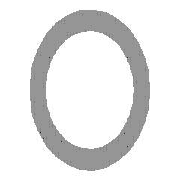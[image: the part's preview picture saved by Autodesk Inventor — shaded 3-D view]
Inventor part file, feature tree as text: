
AUTODESK INVENTOR PART (.ipt)
format: ipt  version: 2021 (Build 250183000, 183)  size: 119,808 bytes
history: native  units: mm (DEFAULTED — no unit token found)
features: other x5, plane x2, sketch x2, sweep x1
ambient origin geometry x8: Origin, YZ Plane, XZ Plane, XY Plane, X Axis, Y Axis, Z Axis, Center Point
bodies: Solid1 (feature_tree)
feature tree (10):
  parser-record x1  (decoder bookkeeping rows leaked as tree rows — omitted from the tree; the rows remain in map.json)
  other  "Driven Length"
  other  "Plano inicial"
  other  "Plano final"
  other  "Trayectoria de barrido"
  plane  "Plano de trabajo de orientación"
  sweep  "Cuerpo"
  sketch  "Sketch3"  dims[d0=42.164mm d1=3.556mm]
  plane  "Work Plane3"
  sketch  "Sketch4"  dims[d4=-0.0mm d5=30.0mm d6=90.0deg d7=30.0mm d8=0.0mm d9=0.0mm]
